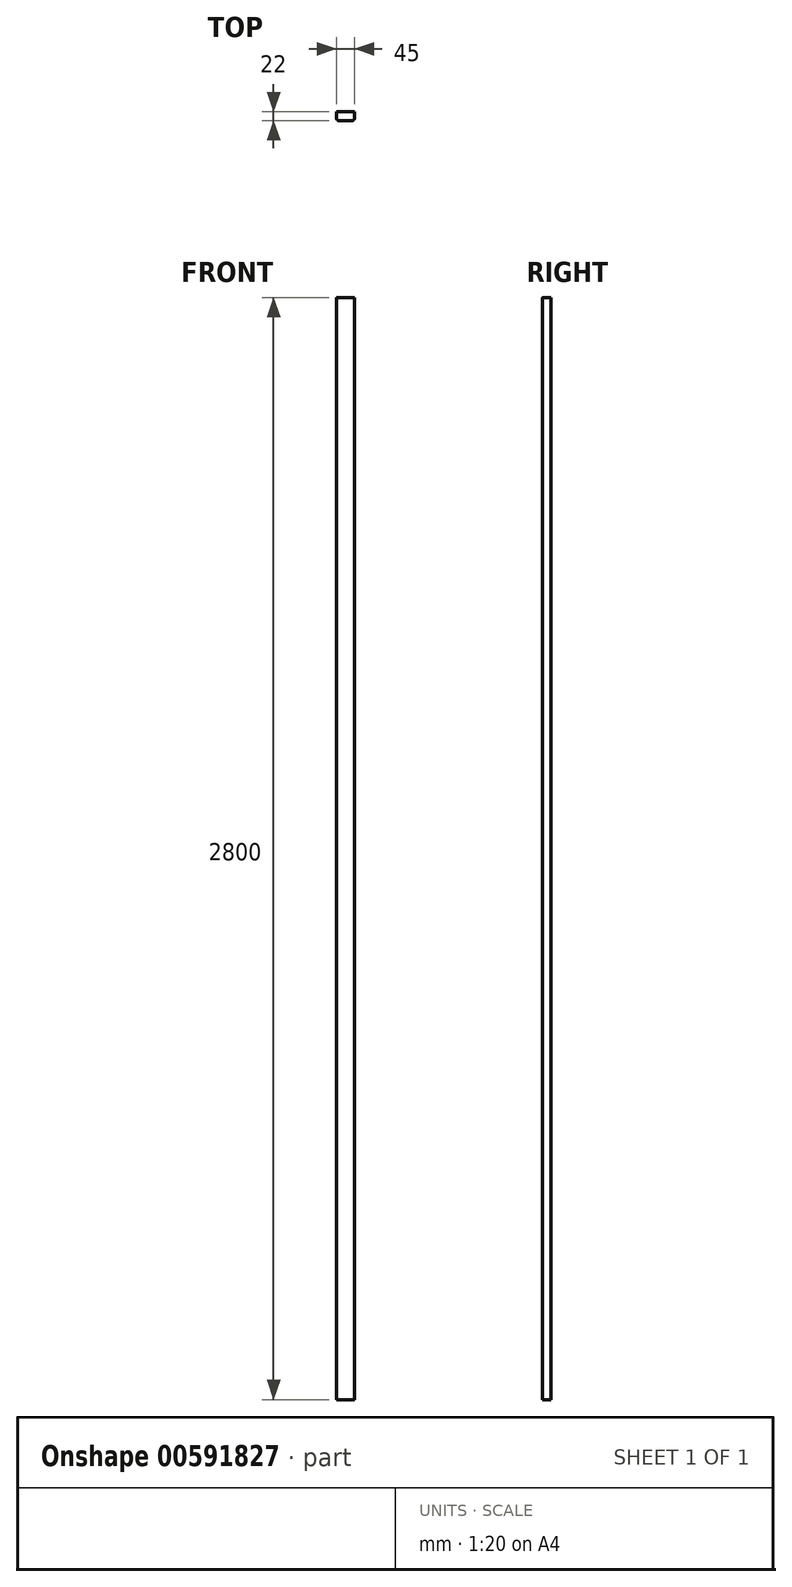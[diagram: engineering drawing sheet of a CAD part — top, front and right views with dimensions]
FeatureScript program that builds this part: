
annotation { "Feature Type Name" : "Feature", "Feature Type Description" : "" }
export const myFeature = defineFeature(function(context is Context, id is Id, definition is map)
    precondition{}
    {
        {
            var Q0;
            Q0=qCreatedBy(makeId("Top.planeOp"),FACE);
            var sketch = newSketch(context, id + "F0", { "sketchPlane" : qUnion([Q0])});
            skLineSegment(sketch, "E0.bottom", {"start": v(5, 0) * mm, "end": v(40, 0) * mm});
            skLineSegment(sketch, "E0.top", {"start": v(0, 22) * mm, "end": v(45, 22) * mm});
            skLineSegment(sketch, "E0.left", {"start": v(0, 5) * mm, "end": v(0, 22) * mm});
            skLineSegment(sketch, "E0.right", {"start": v(45, 5) * mm, "end": v(45, 22) * mm});
            skPoint(sketch, "E1.visualSharp", {"position": v(0, 0) * mm});
            skArc(sketch, "E1.filletArc", {"start": v(0, 5) * mm, "mid": v(1.46, 1.46) * mm, "end": v(5, 0) * mm});
            skPoint(sketch, "E2.visualSharp", {"position": v(45, 0) * mm});
            skArc(sketch, "E2.filletArc", {"start": v(40, 0) * mm, "mid": v(43.54, 1.46) * mm, "end": v(45, 5) * mm});
            skSolve(sketch);
        }
        {
            var Q0;
            Q0=makeQuery(id+"F0.imprint","IMPRINT",FACE,{"disambiguationData":[TD([[makeQuery(id+"F0.imprint","IMPRINT",EDGE,{"derivedFrom":sQuery(id+"F0.wireOp",EDGE,"E0.bottom")}),1.0]])]});
            extrude(context, id + "F1", {"entities" : qUnion([Q0]), "depth" : 2800 * mm, "offsetDistance" : 25 * mm});
        }
    });
